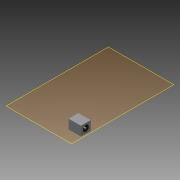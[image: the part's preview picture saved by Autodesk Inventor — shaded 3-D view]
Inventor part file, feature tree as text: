
AUTODESK INVENTOR PART (.ipt)
format: ipt  version: 2013 SP2 (Build 170200200, 200)  size: 95,232 bytes
history: native  units: mm
features: extrude x2, sketch x2, plane x1
ambient origin geometry x8: Origin, YZ Plane, XZ Plane, XY Plane, X Axis, Y Axis, Z Axis, Center Point
bodies: Solid1 (feature_tree)
feature tree (5):
  plane  "Work Plane1"
  extrude  "Extrusion1"  Depth=10.5mm
  extrude  "Extrusion2"  Depth=6.5mm
  sketch  "Sketch1"  dims[d0=13.2mm d2=10.5mm]
  sketch  "Sketch2"  dims[d3=10.0mm d4=0.0mm d5=6.5mm d7=1.5mm d8=10.0mm d9=0.0mm]
